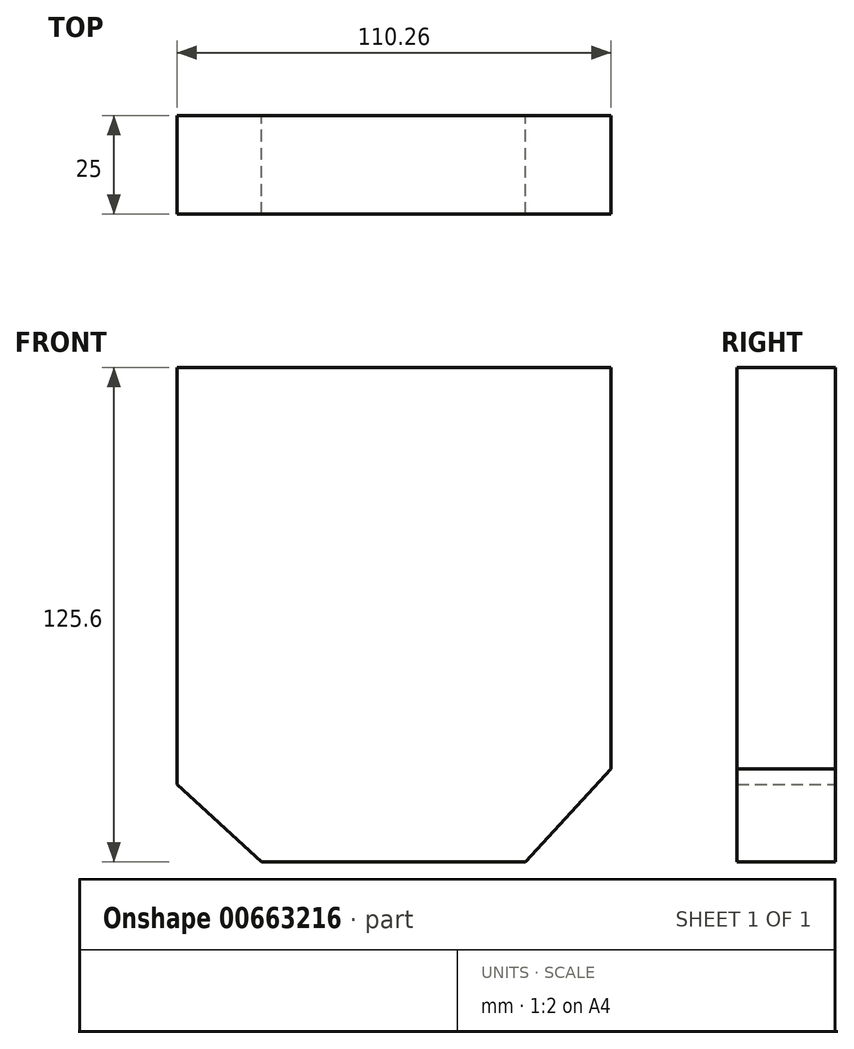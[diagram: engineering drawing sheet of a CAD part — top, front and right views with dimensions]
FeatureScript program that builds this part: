
annotation { "Feature Type Name" : "Feature", "Feature Type Description" : "" }
export const myFeature = defineFeature(function(context is Context, id is Id, definition is map)
    precondition{}
    {
        {
            var Q0;
            Q0=qCreatedBy(makeId("Front.planeOp"),FACE);
            var sketch = newSketch(context, id + "F0", { "sketchPlane" : qUnion([Q0])});
            skLineSegment(sketch, "E0.bottom", {"start": v(-95.76, 33.88) * mm, "end": v(24.5, 33.88) * mm});
            skLineSegment(sketch, "E0.top", {"start": v(-71.26, -101.72) * mm, "end": v(0, -101.72) * mm});
            skLineSegment(sketch, "E0.left", {"start": v(-95.76, 33.88) * mm, "end": v(-95.76, -79.22) * mm});
            skLineSegment(sketch, "E0.right", {"start": v(24.5, 33.88) * mm, "end": v(24.5, -75) * mm});
            skLineSegment(sketch, "E1", {"start": v(-95.76, -79.22) * mm, "end": v(-71.26, -101.72) * mm});
            skLineSegment(sketch, "E2", {"start": v(0, -101.72) * mm, "end": v(24.5, -75) * mm});
            skSolve(sketch);
        }
        {
            var Q0;
            Q0=makeQuery(id+"F0.imprint","IMPRINT",FACE,{"disambiguationData":[TD([[makeQuery(id+"F0.imprint","IMPRINT",EDGE,{"derivedFrom":sQuery(id+"F0.wireOp",EDGE,"E0.bottom")}),-1.0]])]});
            var sketch = newSketch(context, id + "F1", { "sketchPlane" : qUnion([Q0])});
            skLineSegment(sketch, "E3.0", {"start": v(-90.76, 28.88) * mm, "end": v(-90.76, -77.02) * mm});
            skLineSegment(sketch, "E3.1", {"start": v(-69.31, -96.72) * mm, "end": v(-2.2, -96.72) * mm});
            skLineSegment(sketch, "E3.2", {"start": v(-2.2, -96.72) * mm, "end": v(19.5, -73.06) * mm});
            skLineSegment(sketch, "E3.3", {"start": v(-90.76, -77.02) * mm, "end": v(-69.31, -96.72) * mm});
            skLineSegment(sketch, "E3.4", {"start": v(19.5, -73.06) * mm, "end": v(19.5, 28.88) * mm});
            skLineSegment(sketch, "E3.5", {"start": v(19.5, 28.88) * mm, "end": v(-90.76, 28.88) * mm});
            skSolve(sketch);
        }
        {
            var Q0;
            Q0 = qSketchRegion(id + "F1", true);
            var Q1;
            Q1 = qConstructionFilter(qBodyType(qCreatedBy(id + "F1" ,EDGE), BodyType.WIRE), ConstructionObject.NO);
            extrude(context, id + "F2", {"entities" : qUnion([Q0]), "surfaceEntities" : qUnion([Q1]), "depth" : 25 * mm, "offsetDistance" : 25 * mm});
        }
    });
